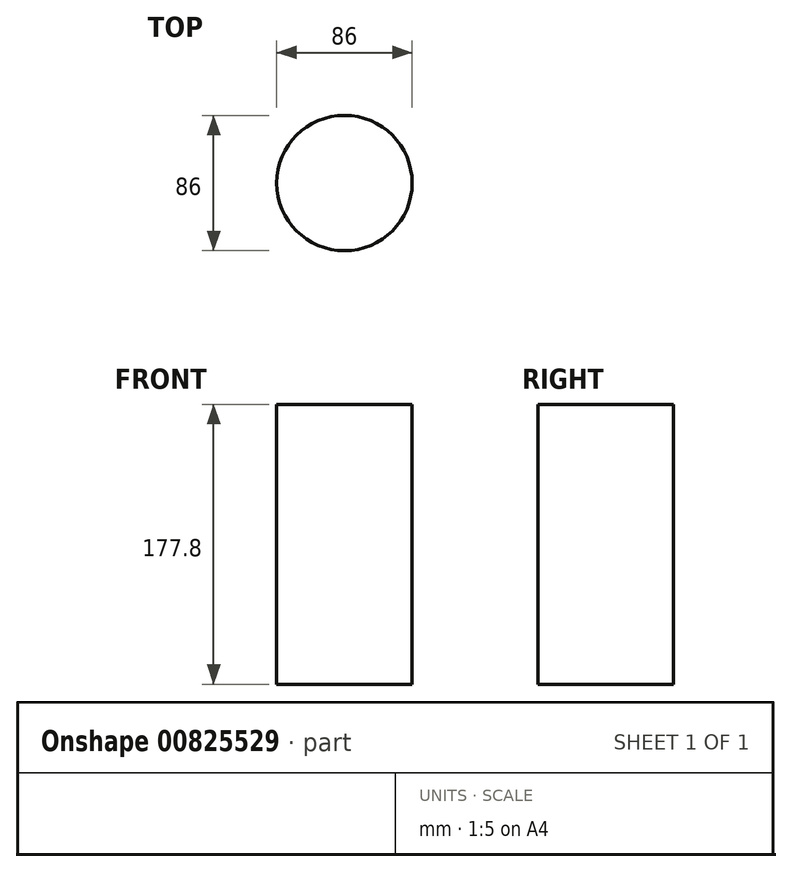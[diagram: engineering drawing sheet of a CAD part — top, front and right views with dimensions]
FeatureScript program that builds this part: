
annotation { "Feature Type Name" : "Feature", "Feature Type Description" : "" }
export const myFeature = defineFeature(function(context is Context, id is Id, definition is map)
    precondition{}
    {
        {
            var Q0;
            Q0=qCreatedBy(makeId("Top.planeOp"),FACE);
            var sketch = newSketch(context, id + "F0", { "sketchPlane" : qUnion([Q0])});
            skCircle(sketch, "E0", {"center": v(0, 0) * mm, "radius": 43 * mm});
            skSolve(sketch);
        }
        {
            var Q0;
            Q0=sQuery(id+"F0.wireOp",EDGE,"E0");
            extrude(context, id + "F1", {"bodyType" : ToolBodyType.SURFACE, "surfaceEntities" : qUnion([Q0]), "depth" : 177.8 * mm, "offsetDistance" : 25.4 * mm});
        }
    });
